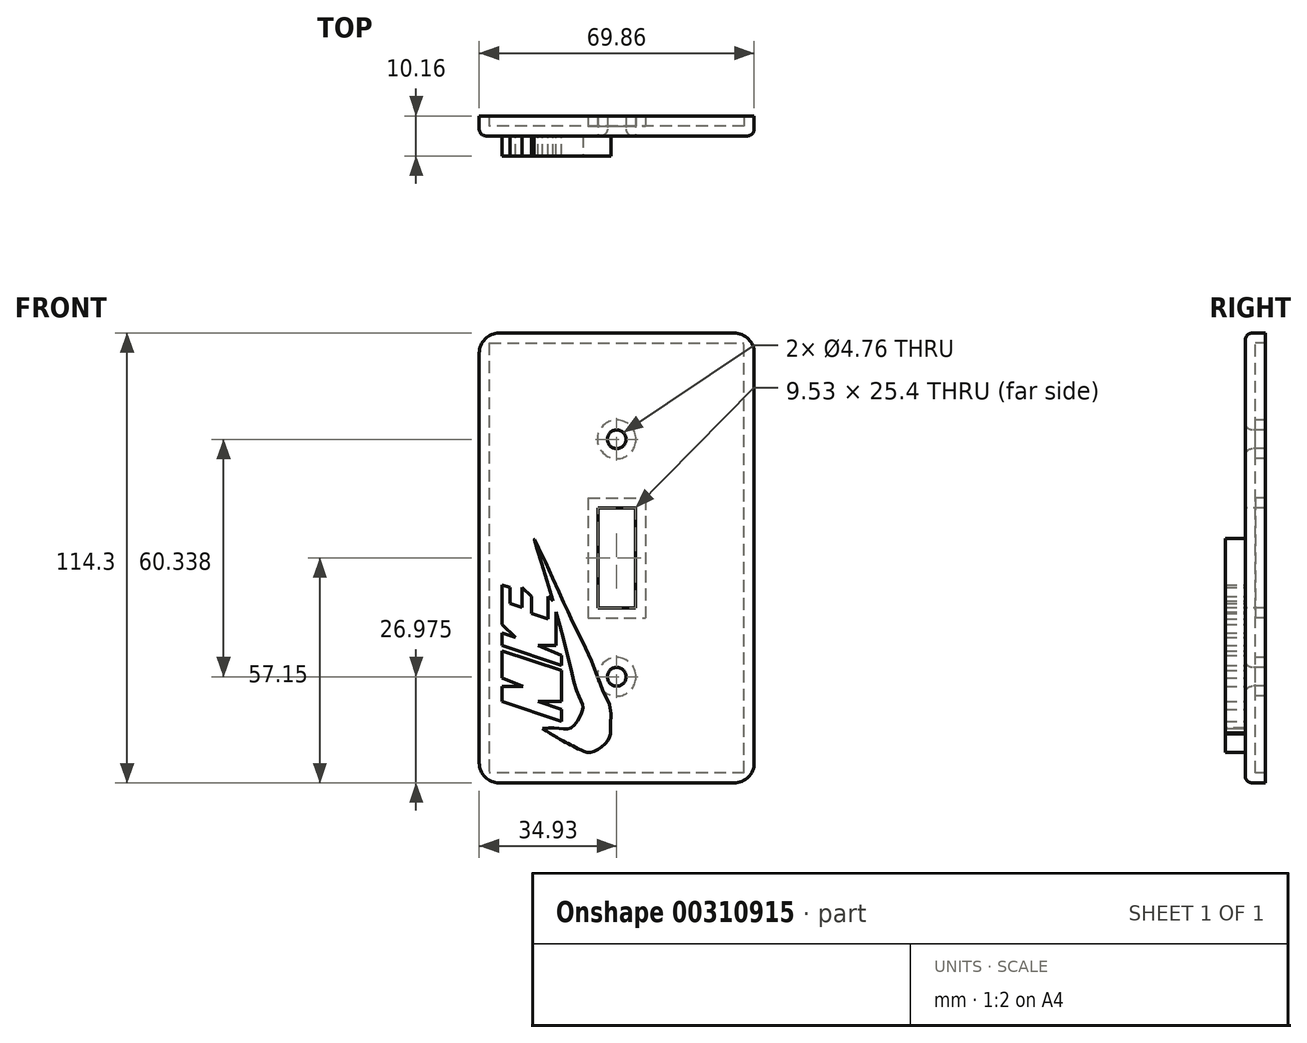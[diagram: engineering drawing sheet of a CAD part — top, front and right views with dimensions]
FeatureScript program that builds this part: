
annotation { "Feature Type Name" : "Feature", "Feature Type Description" : "" }
export const myFeature = defineFeature(function(context is Context, id is Id, definition is map)
    precondition{}
    {
        {
            var Q0;
            Q0=qCreatedBy(makeId("Front.planeOp"),FACE);
            var sketch = newSketch(context, id + "F0", { "sketchPlane" : qUnion([Q0])});
            skLineSegment(sketch, "E0", {"start": v(39.32, 0) * mm, "end": v(-40.27, 0) * mm});
            skLineSegment(sketch, "E1", {"start": v(0, 57.15) * mm, "end": v(0, -57.15) * mm});
            skCircle(sketch, "E2", {"center": v(0, 30.16) * mm, "radius": 2.38 * mm});
            skCircle(sketch, "E3", {"center": v(0, -30.18) * mm, "radius": 2.38 * mm});
            skLineSegment(sketch, "E4", {"start": v(-34.93, 57.15) * mm, "end": v(34.92, 57.15) * mm});
            skLineSegment(sketch, "E5", {"start": v(34.93, -57.15) * mm, "end": v(34.92, 57.15) * mm});
            skLineSegment(sketch, "E6", {"start": v(-34.93, 57.15) * mm, "end": v(-34.92, -57.15) * mm});
            skLineSegment(sketch, "E7", {"start": v(34.93, -57.15) * mm, "end": v(-34.92, -57.15) * mm});
            skLineSegment(sketch, "E8.bottom", {"start": v(-4.76, 12.7) * mm, "end": v(4.76, 12.7) * mm});
            skLineSegment(sketch, "E8.top", {"start": v(-4.76, -12.7) * mm, "end": v(4.76, -12.7) * mm});
            skLineSegment(sketch, "E8.left", {"start": v(-4.76, 12.7) * mm, "end": v(-4.76, -12.7) * mm});
            skLineSegment(sketch, "E8.right", {"start": v(4.76, 12.7) * mm, "end": v(4.76, -12.7) * mm});
            skSolve(sketch);
        }
        {
            var Q0;
            {var subQ8=sQuery(id+"F0.wireOp",EDGE,"E0");var subQ12=sQuery(id+"F0.wireOp",EDGE,"E6");var subQ13=makeQuery(id+"F0.imprint","INTERSECT",VERTEX,{"derivedFrom":[subQ8,subQ12]});Q0=makeQuery(id+"F0.imprint","IMPRINT",FACE,{"disambiguationData":[TD([[makeQuery(id+"F0.imprint","IMPRINT",EDGE,{"disambiguationData":[TD([[subQ13,1.0]])],"derivedFrom":subQ8}),-1.0]])]});}
            var sketch = newSketch(context, id + "F1", { "sketchPlane" : qUnion([Q0])});
            skLineSegment(sketch, "E9", {"start": v(-14.04, -41.55) * mm, "end": v(-29.12, -36.4) * mm});
            skLineSegment(sketch, "E10", {"start": v(-29.12, -36.4) * mm, "end": v(-29.12, -32.58) * mm});
            skLineSegment(sketch, "E11", {"start": v(-29.12, -32.58) * mm, "end": v(-23.77, -32.58) * mm});
            skLineSegment(sketch, "E12", {"start": v(-23.77, -32.58) * mm, "end": v(-29.12, -30.48) * mm});
            skLineSegment(sketch, "E13", {"start": v(-29.12, -30.48) * mm, "end": v(-29.12, -27.61) * mm});
            skLineSegment(sketch, "E14", {"start": v(-29.12, -27.61) * mm, "end": v(-14.04, -32.58) * mm});
            skLineSegment(sketch, "E15", {"start": v(-14.04, -32.58) * mm, "end": v(-14.04, -35.06) * mm});
            skLineSegment(sketch, "E16", {"start": v(-14.04, -35.06) * mm, "end": v(-14.04, -36.4) * mm});
            skLineSegment(sketch, "E17", {"start": v(-14.04, -36.4) * mm, "end": v(-19.95, -36.4) * mm});
            skLineSegment(sketch, "E18", {"start": v(-19.95, -36.4) * mm, "end": v(-14.04, -38.5) * mm});
            skLineSegment(sketch, "E19", {"start": v(-14.04, -38.5) * mm, "end": v(-14.04, -41.55) * mm});
            skLineSegment(sketch, "E20", {"start": v(-29.12, -27.61) * mm, "end": v(-29.12, -23.6) * mm});
            skLineSegment(sketch, "E21", {"start": v(-29.12, -23.6) * mm, "end": v(-14.04, -28.57) * mm});
            skLineSegment(sketch, "E22", {"start": v(-14.04, -28.57) * mm, "end": v(-14.04, -32.58) * mm});
            skLineSegment(sketch, "E23", {"start": v(-14.04, -32.58) * mm, "end": v(-29.12, -26.09) * mm});
            skPoint(sketch, "E23.endSnap0", {"position": v(-21.58, -26.09) * mm});
            skLineSegment(sketch, "E24", {"start": v(-29.12, -22.27) * mm, "end": v(-14.04, -27.23) * mm});
            skLineSegment(sketch, "E25", {"start": v(-29.12, -22.27) * mm, "end": v(-29.12, -19.02) * mm});
            skLineSegment(sketch, "E26", {"start": v(-29.12, -19.02) * mm, "end": v(-25.7, -20.24) * mm});
            skLineSegment(sketch, "E27", {"start": v(-25.7, -20.24) * mm, "end": v(-29.12, -16.92) * mm});
            skLineSegment(sketch, "E28", {"start": v(-29.12, -16.92) * mm, "end": v(-29.12, -14.06) * mm});
            skLineSegment(sketch, "E29", {"start": v(-29.12, -14.06) * mm, "end": v(-24, -19.02) * mm});
            skLineSegment(sketch, "E30", {"start": v(-24, -19.02) * mm, "end": v(-15.37, -19.02) * mm});
            skLineSegment(sketch, "E31", {"start": v(-15.37, -19.02) * mm, "end": v(-15.37, -22.27) * mm});
            skLineSegment(sketch, "E32", {"start": v(-15.37, -22.27) * mm, "end": v(-19.95, -22.27) * mm});
            skLineSegment(sketch, "E33", {"start": v(-19.95, -22.27) * mm, "end": v(-14.04, -24.81) * mm});
            skLineSegment(sketch, "E34", {"start": v(-14.04, -24.81) * mm, "end": v(-14.04, -27.23) * mm});
            skLineSegment(sketch, "E35", {"start": v(-15.37, -19.02) * mm, "end": v(-29.12, -14.06) * mm});
            skLineSegment(sketch, "E36", {"start": v(-29.12, -6.8) * mm, "end": v(-29.12, -14.06) * mm});
            skLineSegment(sketch, "E37", {"start": v(-29.12, -6.8) * mm, "end": v(-27.12, -7.46) * mm});
            skLineSegment(sketch, "E38", {"start": v(-27.12, -7.46) * mm, "end": v(-27.12, -11.57) * mm});
            skLineSegment(sketch, "E39", {"start": v(-27.12, -11.57) * mm, "end": v(-24.1, -12.56) * mm});
            skLineSegment(sketch, "E40", {"start": v(-24.1, -12.56) * mm, "end": v(-24.1, -7.46) * mm});
            skLineSegment(sketch, "E41", {"start": v(-24.1, -7.46) * mm, "end": v(-21.66, -9.83) * mm});
            skLineSegment(sketch, "E42", {"start": v(-21.66, -9.83) * mm, "end": v(-21.66, -14.06) * mm});
            skLineSegment(sketch, "E43", {"start": v(-21.66, -14.06) * mm, "end": v(-17.42, -15.45) * mm});
            skLineSegment(sketch, "E44", {"start": v(-17.42, -15.45) * mm, "end": v(-17.42, -9.83) * mm});
            skLineSegment(sketch, "E45", {"start": v(-15.37, -19.02) * mm, "end": v(-15.37, -11.57) * mm});
            skLineSegment(sketch, "E46", {"start": v(-15.37, -11.57) * mm, "end": v(-17.42, -9.83) * mm});
            skFitSpline(sketch, "E47", {"points": [v(-18.8, -43.27) * mm, v(-13.27, -46.7) * mm, v(-10.22, -48.24) * mm, v(-5.82, -49.2) * mm, v(-1.62, -44.42) * mm], "startDerivative": vector(23.89, -15.35) * mm, "endDerivative": vector(-3.72, 13.31) * mm});
            skPoint(sketch, "E48.10.internal.snap0", {"position": v(-15.37, -15.3) * mm});
            skPoint(sketch, "E48.11.internal.snap0", {"position": v(-15.37, -15.3) * mm});
            skFitSpline(sketch, "E48", {"points": [v(-18.8, -43.27) * mm, v(-14.32, -43.27) * mm, v(-11.84, -43.27) * mm, v(-9.55, -40.67) * mm, v(-8.78, -38.76) * mm, v(-8.6, -37.62) * mm, v(-9.74, -34.94) * mm, v(-13.94, -19.02) * mm, v(-20.62, 3.63) * mm, v(-21, 4.96) * mm, v(-15.37, -7.07) * mm, v(-11.65, -15.3) * mm, v(-5.73, -27.88) * mm, v(-3.25, -34.37) * mm, v(-1.62, -38) * mm, v(-1.62, -44.42) * mm, v(-1.28, -45.65) * mm], "startDerivative": vector(87.55, 4.04) * mm, "endDerivative": vector(15.42, -30.96) * mm});
            skSolve(sketch);
        }
        {
            var Q0;
            Q0 = qSketchRegion(id + "F1", true);
            extrude(context, id + "F2", {"entities" : qUnion([Q0]), "depth" : 5.08 * mm});
        }
        {
            var Q0;
            Q0 = qSketchRegion(id + "F0", true);
            extrude(context, id + "F3", {"entities" : qUnion([Q0]), "oppositeDirection" : true, "depth" : 5.08 * mm});
        }
        {
            var Q0;
            Q0=makeQuery(id+"F3.opExtrude","CAP_EDGE",EDGE,{"disambiguationData":[OSD([sQuery(id+"F0.wireOp",EDGE,"E2")])],"isStart":true});
            var Q1;
            Q1=makeQuery(id+"F3.opExtrude","CAP_EDGE",EDGE,{"disambiguationData":[OSD([sQuery(id+"F0.wireOp",EDGE,"E3")])],"isStart":true});
            fillet(context, id + "F4", {"entities" : qUnion([Q0, Q1]), "radius" : 1.78 * mm, "tangentPropagation" : true, "allowEdgeOverflow" : false});
        }
        {
            var Q0;
            Q0=makeQuery(id+"F3.opExtrude","CAP_EDGE",EDGE,{"disambiguationData":[OSD([sQuery(id+"F0.wireOp",EDGE,"E4")])],"isStart":true});
            var Q1;
            Q1=makeQuery(id+"F3.opExtrude","CAP_EDGE",EDGE,{"disambiguationData":[OSD([sQuery(id+"F0.wireOp",EDGE,"E5")])],"isStart":true});
            var Q2;
            Q2=makeQuery(id+"F3.opExtrude","CAP_EDGE",EDGE,{"disambiguationData":[OSD([sQuery(id+"F0.wireOp",EDGE,"E6")])],"isStart":true});
            var Q3;
            Q3=makeQuery(id+"F3.opExtrude","CAP_EDGE",EDGE,{"disambiguationData":[OSD([sQuery(id+"F0.wireOp",EDGE,"E7")])],"isStart":true});
            fillet(context, id + "F5", {"entities" : qUnion([Q0, Q1, Q2, Q3]), "radius" : 1.78 * mm, "tangentPropagation" : true, "allowEdgeOverflow" : false});
        }
        {
            var Q0;
            Q0=makeQuery(id+"F3.opExtrude","CAP_FACE",FACE,{"disambiguationData":[OSD([sQuery(id+"F0.wireOp",EDGE,"E2"),sQuery(id+"F0.wireOp",EDGE,"E3"),sQuery(id+"F0.wireOp",EDGE,"E4"),sQuery(id+"F0.wireOp",EDGE,"E5"),sQuery(id+"F0.wireOp",EDGE,"E6"),sQuery(id+"F0.wireOp",EDGE,"E7"),sQuery(id+"F0.wireOp",EDGE,"E8.bottom"),sQuery(id+"F0.wireOp",EDGE,"E8.top"),sQuery(id+"F0.wireOp",EDGE,"E8.left"),sQuery(id+"F0.wireOp",EDGE,"E8.right")])],"isStart":false});
            shell(context, id + "F6", {"entities" : qUnion([Q0]), "thickness" : 2.54 * mm});
        }
        {
            var Q0;
            Q0=makeQuery(id+"F3.opExtrude","SWEPT_EDGE",EDGE,{"disambiguationData":[OSD([sQuery(id+"F0.wireOp",EDGE,"E4"),sQuery(id+"F0.wireOp",EDGE,"E5")])]});
            var Q1;
            Q1=makeQuery(id+"F3.opExtrude","SWEPT_EDGE",EDGE,{"disambiguationData":[OSD([sQuery(id+"F0.wireOp",EDGE,"E5"),sQuery(id+"F0.wireOp",EDGE,"E7")])]});
            var Q2;
            Q2=makeQuery(id+"F3.opExtrude","SWEPT_EDGE",EDGE,{"disambiguationData":[OSD([sQuery(id+"F0.wireOp",EDGE,"E4"),sQuery(id+"F0.wireOp",EDGE,"E6")])]});
            var Q3;
            Q3=makeQuery(id+"F3.opExtrude","SWEPT_EDGE",EDGE,{"disambiguationData":[OSD([sQuery(id+"F0.wireOp",EDGE,"E6"),sQuery(id+"F0.wireOp",EDGE,"E7")])]});
            fillet(context, id + "F7", {"entities" : qUnion([Q0, Q1, Q2, Q3]), "radius" : 5.08 * mm, "tangentPropagation" : true, "allowEdgeOverflow" : false});
        }
    });
